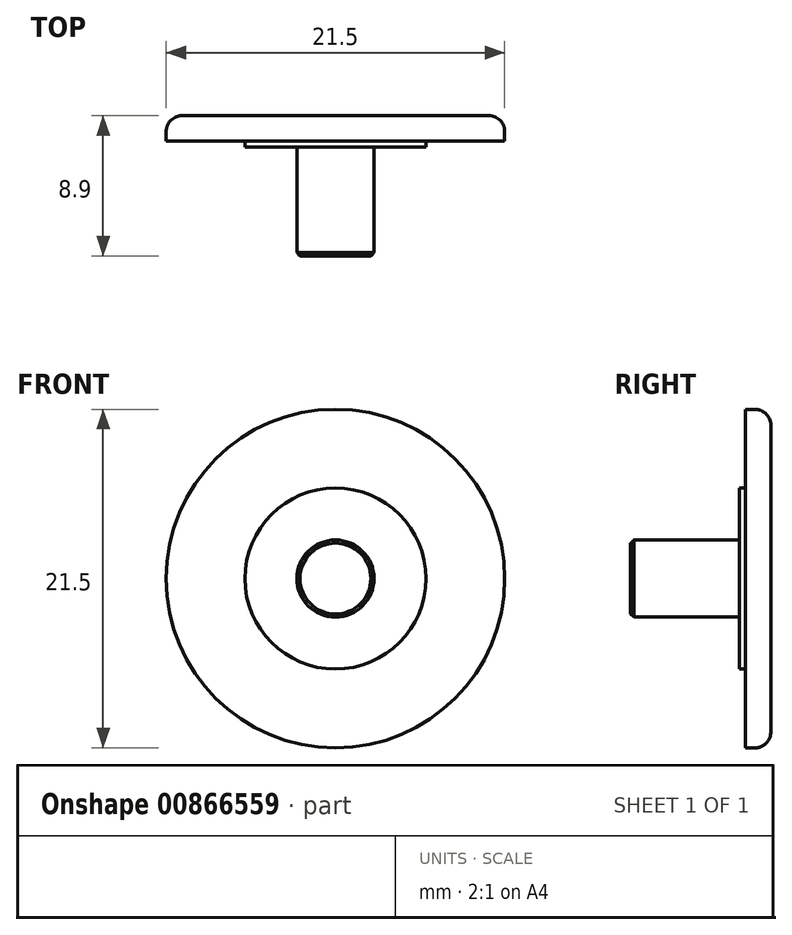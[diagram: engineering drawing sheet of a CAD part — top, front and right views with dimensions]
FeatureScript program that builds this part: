
annotation { "Feature Type Name" : "Feature", "Feature Type Description" : "" }
export const myFeature = defineFeature(function(context is Context, id is Id, definition is map)
    precondition{}
    {
        {
            var Q0;
            Q0=qCreatedBy(makeId("Top.planeOp"),FACE);
            var sketch = newSketch(context, id + "F0", { "sketchPlane" : qUnion([Q0])});
            skLineSegment(sketch, "E0", {"start": v(0, 0) * mm, "end": v(0, 8.9) * mm});
            skLineSegment(sketch, "E1", {"start": v(0, 8.9) * mm, "end": v(9.75, 8.9) * mm});
            skLineSegment(sketch, "E2", {"start": v(10.75, 7.9) * mm, "end": v(10.75, 7.3) * mm});
            skLineSegment(sketch, "E3", {"start": v(10.75, 7.3) * mm, "end": v(5.75, 7.3) * mm});
            skLineSegment(sketch, "E4", {"start": v(5.75, 7.3) * mm, "end": v(5.75, 6.9) * mm});
            skLineSegment(sketch, "E5", {"start": v(5.75, 6.9) * mm, "end": v(2.45, 6.9) * mm});
            skLineSegment(sketch, "E6", {"start": v(2.45, 6.9) * mm, "end": v(2.45, 0) * mm});
            skLineSegment(sketch, "E7", {"start": v(2.45, 0) * mm, "end": v(0, 0) * mm});
            skPoint(sketch, "E8.visualSharp", {"position": v(10.75, 8.9) * mm});
            skArc(sketch, "E8.filletArc", {"start": v(10.75, 7.9) * mm, "mid": v(10.46, 8.6) * mm, "end": v(9.75, 8.9) * mm});
            skSolve(sketch);
        }
        {
            var Q0;
            Q0 = qSketchRegion(id + "F0", true);
            var Q1;
            Q1=sQuery(id+"F0.wireOp",EDGE,"E0");
            revolve(context, id + "F1", {"surfaceOperationType" : NewSurfaceOperationType.NEW, "entities" : qUnion([Q0]), "axis" : qUnion([Q1]), "revolveType" : RevolveType.FULL});
        }
        {
            var Q0;
            Q0=makeQuery(id+"F1.opRevolve","SWEPT_FACE",FACE,{"disambiguationData":[OSD([sQuery(id+"F0.wireOp",EDGE,"E7")])]});
            chamfer(context, id + "F2", {"entities" : qUnion([Q0]), "width" : .2 * mm, "tangentPropagation" : true});
        }
    });
